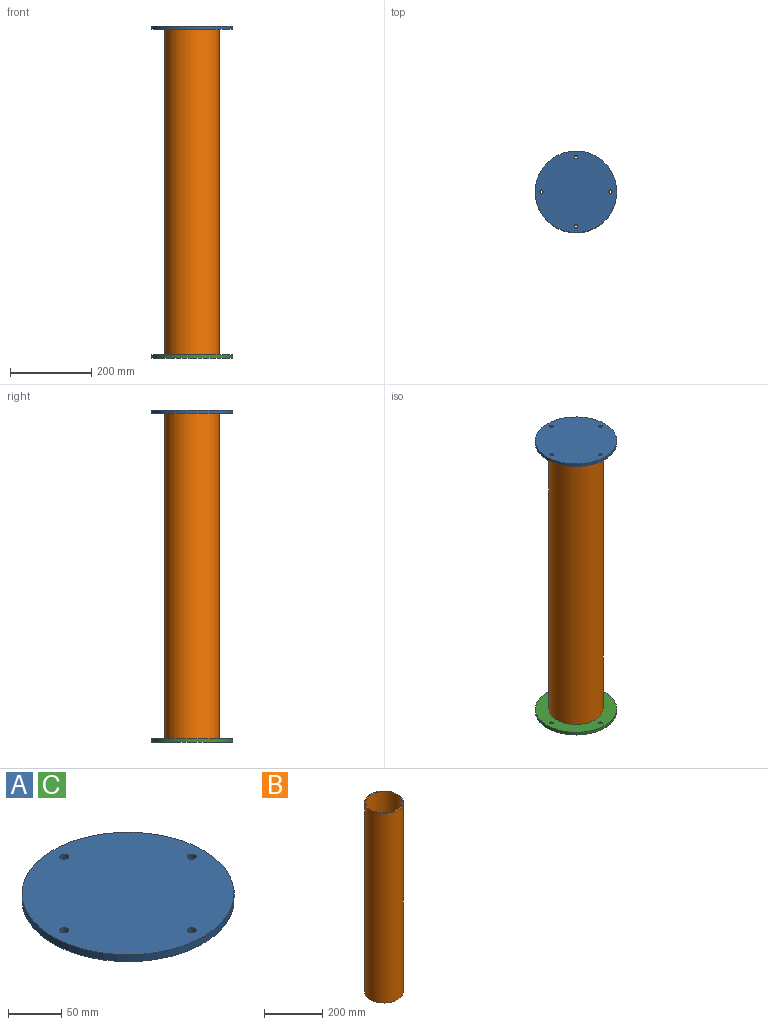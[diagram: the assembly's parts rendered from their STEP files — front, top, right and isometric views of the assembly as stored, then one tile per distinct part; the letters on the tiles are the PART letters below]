
ASSEMBLY  parts=3 mates=1
PART A: 7 faces, bbox 200x200x8 mm
  f0: cylinder r=4.25mm len=8.5mm, axis (0,0,1), area 213.6mm2, adj f5,f6
  f1: cylinder r=4.25mm len=8.5mm, axis (0,0,1), area 213.6mm2, adj f5,f6
  f2: cylinder r=4.25mm len=8.5mm, axis (0,0,1), area 213.6mm2, adj f5,f6
  f3: cylinder r=4.25mm len=8.5mm, axis (0,0,1), area 213.6mm2, adj f5,f6
  f4: cylinder r=100mm len=200mm, axis (0,0,1), area 5026.5mm2, adj f5,f6
  f5: plane 200x200mm, normal (0,0,-1), area 31188.9mm2, adj f0,f1,f2,f3,f4
  f6: plane 200x200mm, normal (0,0,1), area 31188.9mm2, adj f0,f1,f2,f3,f4
PART B: 4 faces, bbox 133x133x800 mm
  f0: cylinder r=63mm len=800mm, axis (0,0,-1), area 316672.5mm2, adj f2,f3
  f1: cylinder r=66.5mm len=800mm, axis (0,0,-1), area 334265.5mm2, adj f2,f3
  f2: plane 133x133mm, normal (0,0,1), area 1423.9mm2, adj f0,f1
  f3: plane 133x133mm, normal (0,0,-1), area 1423.9mm2, adj f0,f1
PART C: same geometry as A
PLACE A t=(0,0,808)mm
PLACE B at identity
PLACE C at identity fixed
MATE fastened A.f4 <-> B.f0  axis (0,0,-1) through (0,0,800)mm
